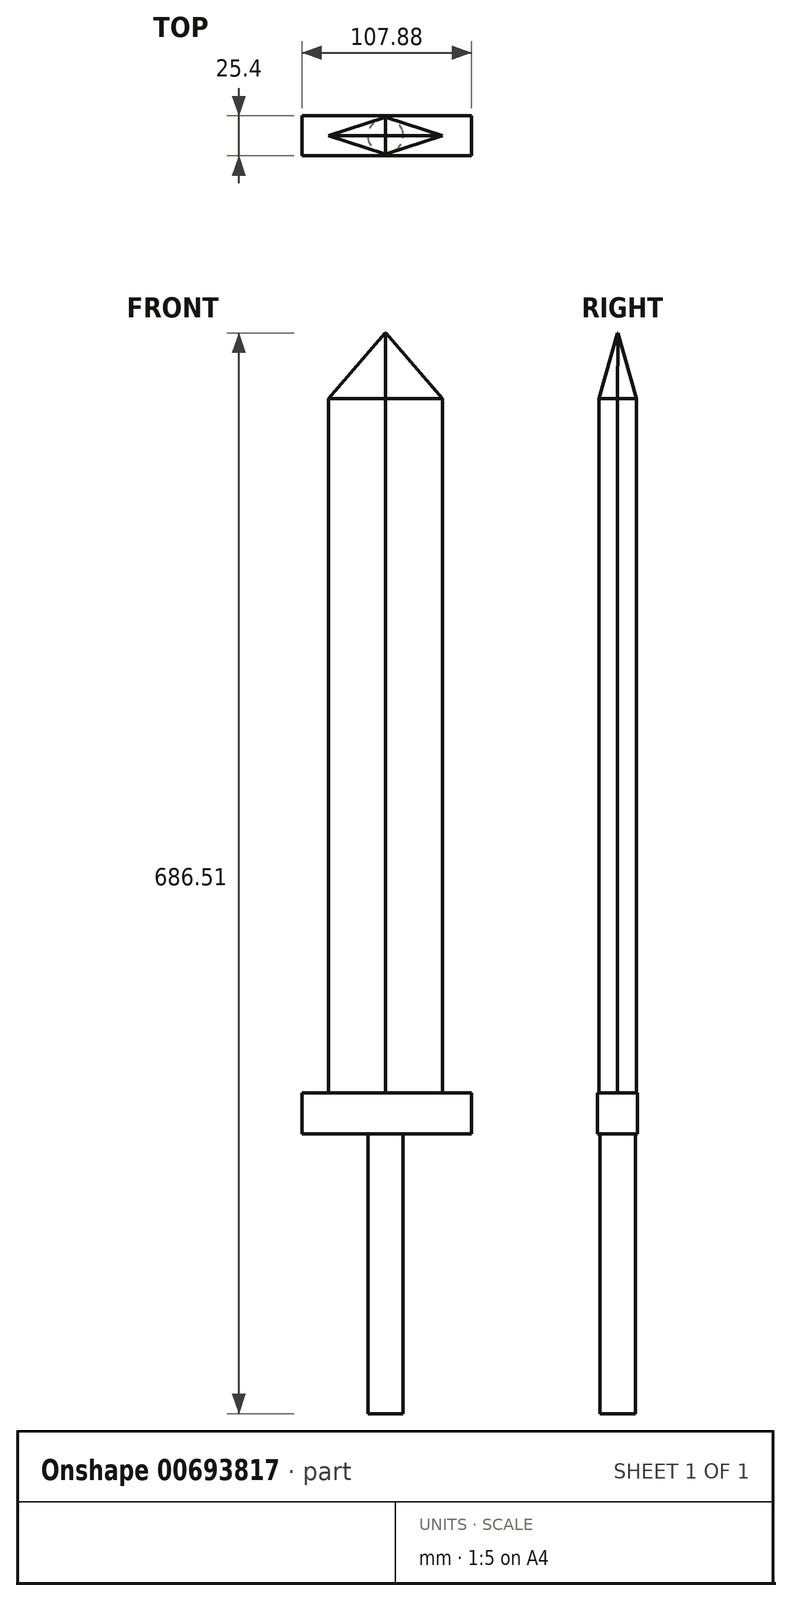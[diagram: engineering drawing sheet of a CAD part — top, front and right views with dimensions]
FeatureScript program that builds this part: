
annotation { "Feature Type Name" : "Feature", "Feature Type Description" : "" }
export const myFeature = defineFeature(function(context is Context, id is Id, definition is map)
    precondition{}
    {
        {
            var Q0;
            Q0=qCreatedBy(makeId("Front.planeOp"),FACE);
            var sketch = newSketch(context, id + "F0", { "sketchPlane" : qUnion([Q0])});
            skLineSegment(sketch, "E0.bottom", {"start": v(-53.15, 13.45) * mm, "end": v(54.73, 13.45) * mm});
            skLineSegment(sketch, "E0.top", {"start": v(-53.15, -12.66) * mm, "end": v(54.73, -12.66) * mm});
            skLineSegment(sketch, "E0.left", {"start": v(-53.15, 13.45) * mm, "end": v(-53.15, -12.66) * mm});
            skLineSegment(sketch, "E0.right", {"start": v(54.73, 13.45) * mm, "end": v(54.73, -12.66) * mm});
            skSolve(sketch);
        }
        {
            var Q0;
            Q0=makeQuery(id+"F0.imprint","IMPRINT",FACE,{"disambiguationData":[TD([[makeQuery(id+"F0.imprint","IMPRINT",EDGE,{"derivedFrom":sQuery(id+"F0.wireOp",EDGE,"E0.bottom")}),-1.0]])]});
            extrude(context, id + "F1", {"entities" : qUnion([Q0]), "depth" : 12.7 * mm, "offsetDistance" : 25.4 * mm});
        }
        {
            var Q0;
            Q0=makeQuery(id+"F1.opExtrude","CAP_FACE",FACE,{"disambiguationData":[OSD([sQuery(id+"F0.wireOp",EDGE,"E0.bottom"),sQuery(id+"F0.wireOp",EDGE,"E0.top"),sQuery(id+"F0.wireOp",EDGE,"E0.left"),sQuery(id+"F0.wireOp",EDGE,"E0.right")])],"isStart":true});
            extrude(context, id + "F2", {"entities" : qUnion([Q0]), "operationType" : NewBodyOperationType.ADD, "depth" : 12.7 * mm, "offsetDistance" : 25.4 * mm});
        }
        {
            var Q0;
            {var subQ0=sQuery(id+"F0.wireOp",EDGE,"E0.top");Q0=makeQuery(id+"F2.boolean.opBoolean","MERGE",FACE,{"derivedFrom":[makeQuery(id+"F1.opExtrude","SWEPT_FACE",FACE,{"disambiguationData":[OSD([subQ0])]}),makeQuery(id+"F2.opExtrude","SWEPT_FACE",FACE,{"disambiguationData":[OSD([subQ0])]})]});}
            var sketch = newSketch(context, id + "F3", { "sketchPlane" : qUnion([Q0])});
            skCircle(sketch, "E1", {"center": v(0, 0) * mm, "radius": 11.22 * mm});
            skSolve(sketch);
        }
        {
            var Q0;
            Q0=makeQuery(id+"F3.imprint","IMPRINT",FACE,{"disambiguationData":[TD([[makeQuery(id+"F3.imprint","IMPRINT",EDGE,{"derivedFrom":sQuery(id+"F3.wireOp",EDGE,"E1")}),1.0]])]});
            extrude(context, id + "F4", {"entities" : qUnion([Q0]), "operationType" : NewBodyOperationType.ADD, "depth" : 177.8 * mm, "offsetDistance" : 25.4 * mm});
        }
        {
            var Q0;
            {var subQ0=sQuery(id+"F0.wireOp",EDGE,"E0.bottom");Q0=makeQuery(id+"F2.boolean.opBoolean","MERGE",FACE,{"derivedFrom":[makeQuery(id+"F1.opExtrude","SWEPT_FACE",FACE,{"disambiguationData":[OSD([subQ0])]}),makeQuery(id+"F2.opExtrude","SWEPT_FACE",FACE,{"disambiguationData":[OSD([subQ0])]})]});}
            var sketch = newSketch(context, id + "F5", { "sketchPlane" : qUnion([Q0])});
            skLineSegment(sketch, "E2", {"start": v(0, 11.87) * mm, "end": v(36.2, 0) * mm});
            skLineSegment(sketch, "E3", {"start": v(36.2, 0) * mm, "end": v(0, -11.73) * mm});
            skLineSegment(sketch, "E4", {"start": v(0, -11.73) * mm, "end": v(-36.23, 0) * mm});
            skLineSegment(sketch, "E5", {"start": v(-36.23, 0) * mm, "end": v(0, 11.87) * mm});
            skSolve(sketch);
        }
        {
            var Q0;
            Q0=makeQuery(id+"F5.imprint","IMPRINT",FACE,{"disambiguationData":[TD([[makeQuery(id+"F5.imprint","IMPRINT",EDGE,{"derivedFrom":sQuery(id+"F5.wireOp",EDGE,"E2")}),-1.0]])]});
            extrude(context, id + "F6", {"entities" : qUnion([Q0]), "operationType" : NewBodyOperationType.ADD, "depth" : 482.6 * mm, "offsetDistance" : 25.4 * mm});
        }
        {
            var Q0;
            Q0=makeQuery(id+"F6.opExtrude","CAP_FACE",FACE,{"disambiguationData":[OSD([sQuery(id+"F5.wireOp",EDGE,"E2"),sQuery(id+"F5.wireOp",EDGE,"E3"),sQuery(id+"F5.wireOp",EDGE,"E4"),sQuery(id+"F5.wireOp",EDGE,"E5")])],"isStart":false});
            chamfer(context, id + "F7", {"entities" : qUnion([Q0]), "chamferType" : ChamferType.OFFSET_ANGLE, "width" : 41.66 * mm, "oppositeDirection" : false, "angle" : 15 * degree, "tangentPropagation" : true});
        }
    });
